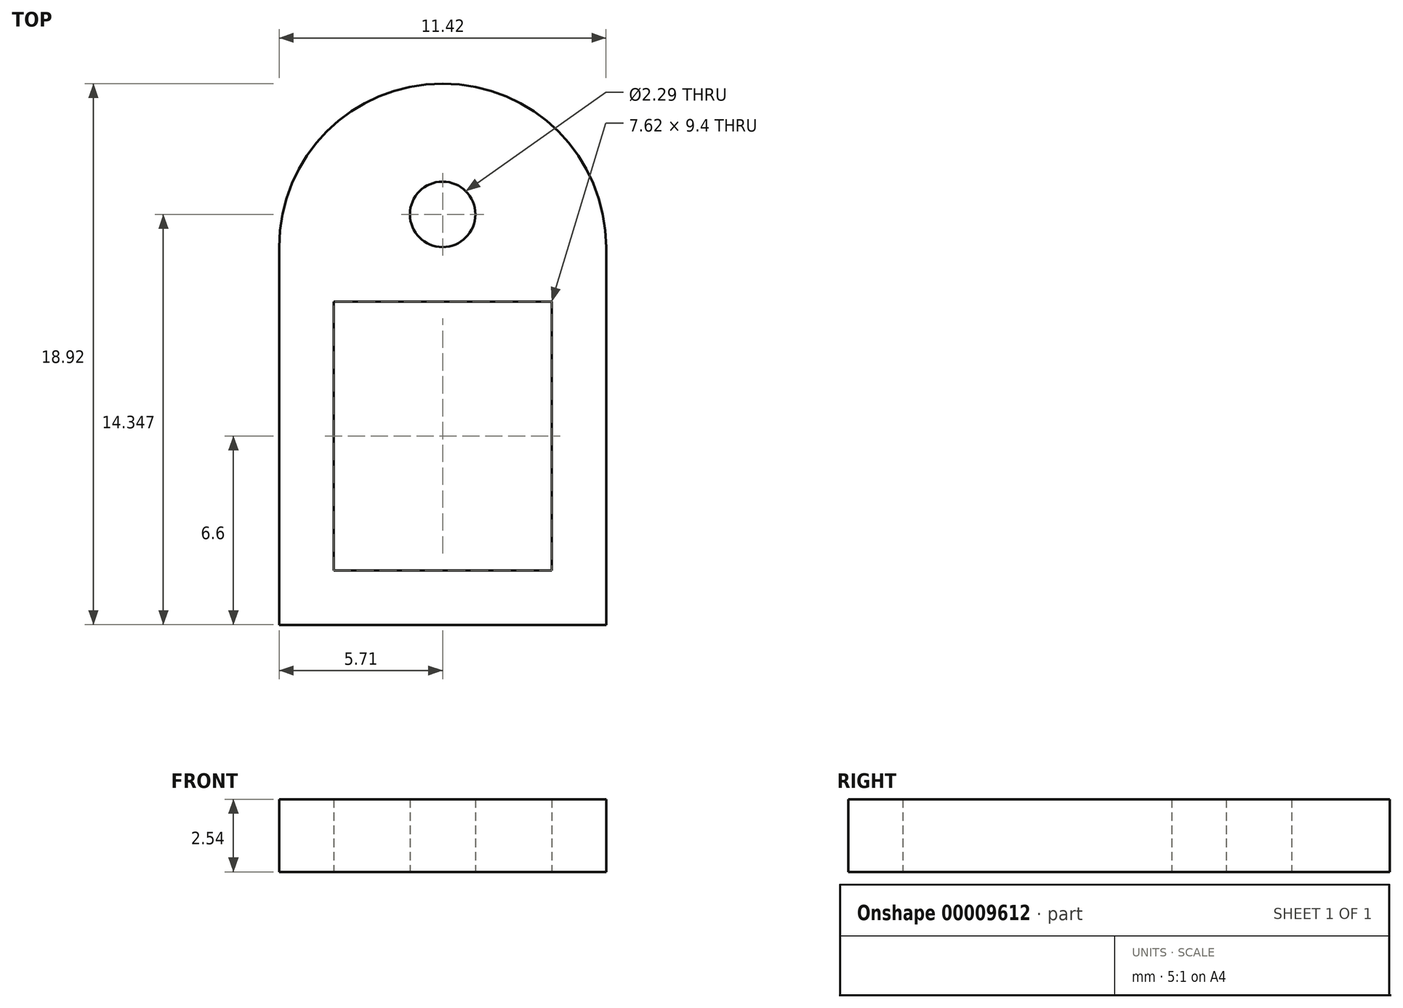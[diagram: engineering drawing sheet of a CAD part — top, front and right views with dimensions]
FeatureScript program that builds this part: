
annotation { "Feature Type Name" : "Feature", "Feature Type Description" : "" }
export const myFeature = defineFeature(function(context is Context, id is Id, definition is map)
    precondition{}
    {
        {
            var Q0;
            Q0=qCreatedBy(makeId("Top.planeOp"),FACE);
            var sketch = newSketch(context, id + "F0", { "sketchPlane" : qUnion([Q0])});
            skLineSegment(sketch, "E0.rect.bottom", {"start": v(3.8, 4.7) * mm, "end": v(-3.81, 4.7) * mm});
            skLineSegment(sketch, "E0.rect.top", {"start": v(3.81, -4.7) * mm, "end": v(-3.8, -4.7) * mm});
            skLineSegment(sketch, "E0.rect.left", {"start": v(3.8, 4.7) * mm, "end": v(3.81, -4.7) * mm});
            skLineSegment(sketch, "E0.rect.right", {"start": v(-3.81, 4.7) * mm, "end": v(-3.8, -4.7) * mm});
            skPoint(sketch, "E0.rect.middle", {"position": v(0, 0) * mm});
            skLineSegment(sketch, "E1.rect.bottom", {"start": v(5.71, 6.6) * mm, "end": v(-5.71, 6.6) * mm});
            skLineSegment(sketch, "E1.rect.top", {"start": v(5.72, -6.6) * mm, "end": v(-5.71, -6.6) * mm});
            skLineSegment(sketch, "E1.rect.left", {"start": v(5.71, 6.6) * mm, "end": v(5.72, -6.6) * mm});
            skLineSegment(sketch, "E1.rect.right", {"start": v(-5.71, 6.6) * mm, "end": v(-5.71, -6.6) * mm});
            skArc(sketch, "E2", {"start": v(5.72, 6.6) * mm, "mid": v(0, 12.32) * mm, "end": v(-5.72, 6.6) * mm});
            skCircle(sketch, "E3", {"center": v(0, 7.75) * mm, "radius": 1.14 * mm});
            skLineSegment(sketch, "E4", {"start": v(-5.71, 0) * mm, "end": v(18.42, 0) * mm, "construction": true});
            skCircle(sketch, "E5.0.MirrorC", {"center": v(0, -7.75) * mm, "radius": 1.14 * mm});
            skArc(sketch, "E5.1.MirrorCS", {"start": v(5.72, -6.6) * mm, "mid": v(0, -12.32) * mm, "end": v(-5.72, -6.6) * mm});
            skSolve(sketch);
        }
        {
            var Q0;
            {var subQ1=sQuery(id+"F0.wireOp",EDGE,"062daad7-31ea-410d-92fb-350fac62528c");Q0=makeQuery(id+"F0.imprint","IMPRINT",FACE,{"disambiguationData":[TD([[makeQuery(id+"F0.imprint","IMPRINT",EDGE,{"derivedFrom":subQ1}),-1.0]])]});}
            var Q1;
            Q1=makeQuery(id+"F0.imprint","IMPRINT",FACE,{"disambiguationData":[TD([[makeQuery(id+"F0.imprint","IMPRINT",EDGE,{"derivedFrom":sQuery(id+"F0.wireOp",EDGE,"E0.rect.bottom")}),-1.0]])]});
            var Q2;
            {var subQ1=sQuery(id+"F0.wireOp",EDGE,"E2");Q2=makeQuery(id+"F0.imprint","IMPRINT",FACE,{"disambiguationData":[TD([[makeQuery(id+"F0.imprint","IMPRINT",EDGE,{"derivedFrom":subQ1}),1.0]])]});}
            var Q3;
            Q3=makeQuery(id+"F0.imprint","IMPRINT",FACE,{"disambiguationData":[TD([[makeQuery(id+"F0.imprint","IMPRINT",EDGE,{"derivedFrom":sQuery(id+"F0.wireOp",EDGE,"023b6f6c-ea11-4d67-b4bb-3a1dc3ada0e5")}),1.0]])]});
            var Q4;
            {var subQ1=sQuery(id+"F0.wireOp",EDGE,"E5.1.MirrorCS");Q4=makeQuery(id+"F0.imprint","IMPRINT",FACE,{"disambiguationData":[TD([[makeQuery(id+"F0.imprint","IMPRINT",EDGE,{"derivedFrom":subQ1}),-1.0]])]});}
            extrude(context, id + "F1", {"entities" : qUnion([Q0, Q1, Q2, Q3, Q4]), "depth" : 2.54 * mm});
        }
    });
